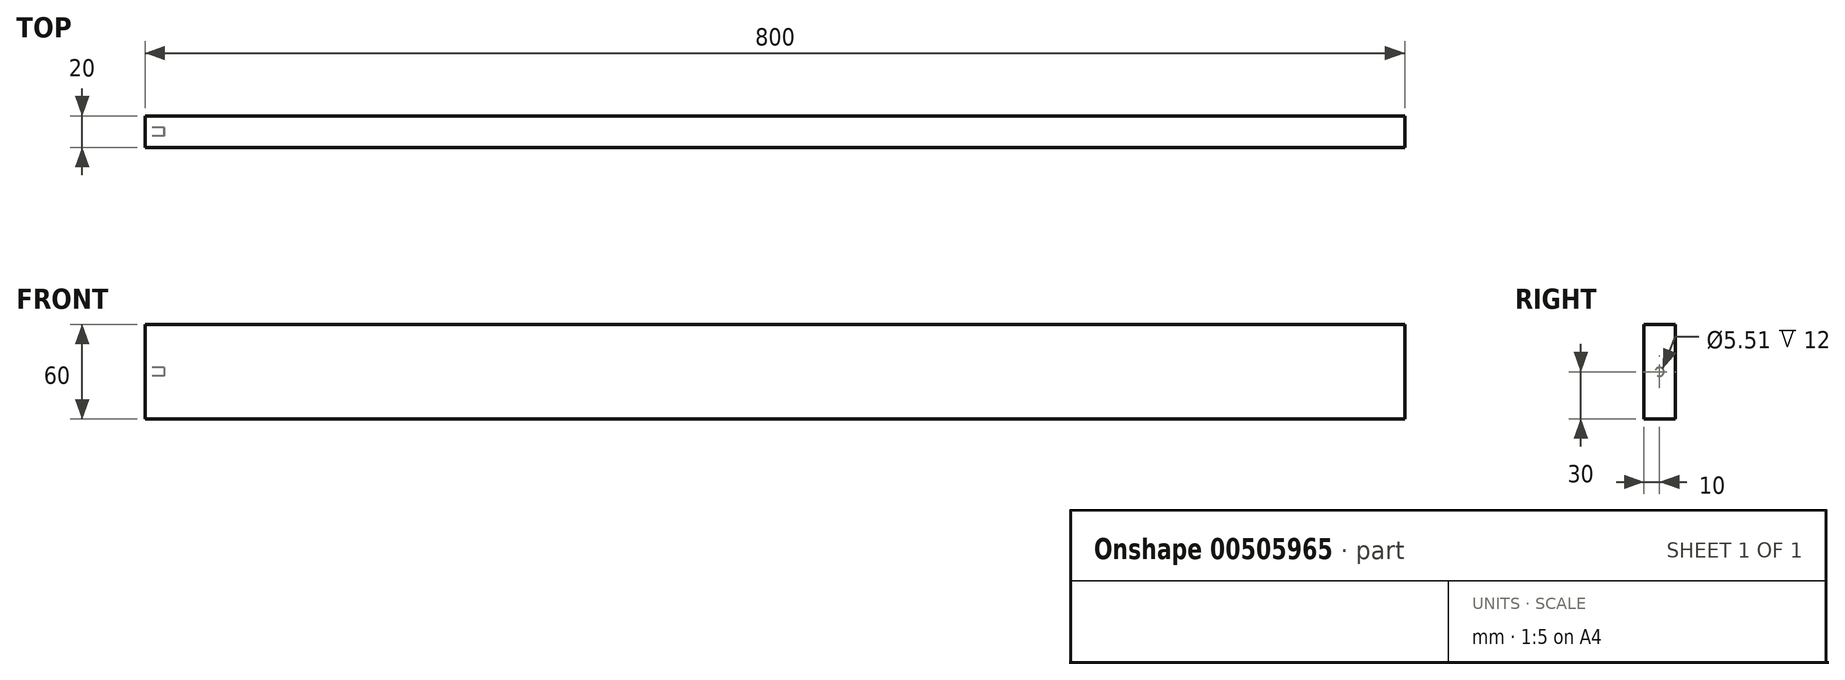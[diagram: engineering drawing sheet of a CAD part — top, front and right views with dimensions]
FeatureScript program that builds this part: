
annotation { "Feature Type Name" : "Feature", "Feature Type Description" : "" }
export const myFeature = defineFeature(function(context is Context, id is Id, definition is map)
    precondition{}
    {
        {
            var Q0;
            Q0=qCreatedBy(makeId("Right.planeOp"),FACE);
            var sketch = newSketch(context, id + "F0", { "sketchPlane" : qUnion([Q0])});
            skLineSegment(sketch, "E0.bottom", {"start": v(0, 0) * mm, "end": v(20, 0) * mm});
            skLineSegment(sketch, "E0.top", {"start": v(0, 60) * mm, "end": v(20, 60) * mm});
            skLineSegment(sketch, "E0.left", {"start": v(0, 0) * mm, "end": v(0, 60) * mm});
            skLineSegment(sketch, "E0.right", {"start": v(20, 0) * mm, "end": v(20, 60) * mm});
            skSolve(sketch);
        }
        {
            var Q0;
            Q0 = qSketchRegion(id + "F0", true);
            extrude(context, id + "F1", {"entities" : qUnion([Q0]), "depth" : 800 * mm, "offsetDistance" : 25 * mm, "symmetric" : true});
        }
        {
            var Q0;
            Q0=makeQuery(id+"F1.opExtrude","CAP_FACE",FACE,{"disambiguationData":[OSD([sQuery(id+"F0.wireOp",EDGE,"E0.bottom"),sQuery(id+"F0.wireOp",EDGE,"E0.top"),sQuery(id+"F0.wireOp",EDGE,"E0.left"),sQuery(id+"F0.wireOp",EDGE,"E0.right")])],"isStart":true});
            var sketch = newSketch(context, id + "F2", { "sketchPlane" : qUnion([Q0])});
            skCircle(sketch, "E1", {"center": v(-10, 30) * mm, "radius": 2.76 * mm});
            skSolve(sketch);
        }
        {
            var Q0;
            Q0 = qSketchRegion(id + "F2", true);
            extrude(context, id + "F3", {"entities" : qUnion([Q0]), "operationType" : NewBodyOperationType.REMOVE, "oppositeDirection" : true, "depth" : 12 * mm, "offsetDistance" : 25 * mm});
        }
    });
